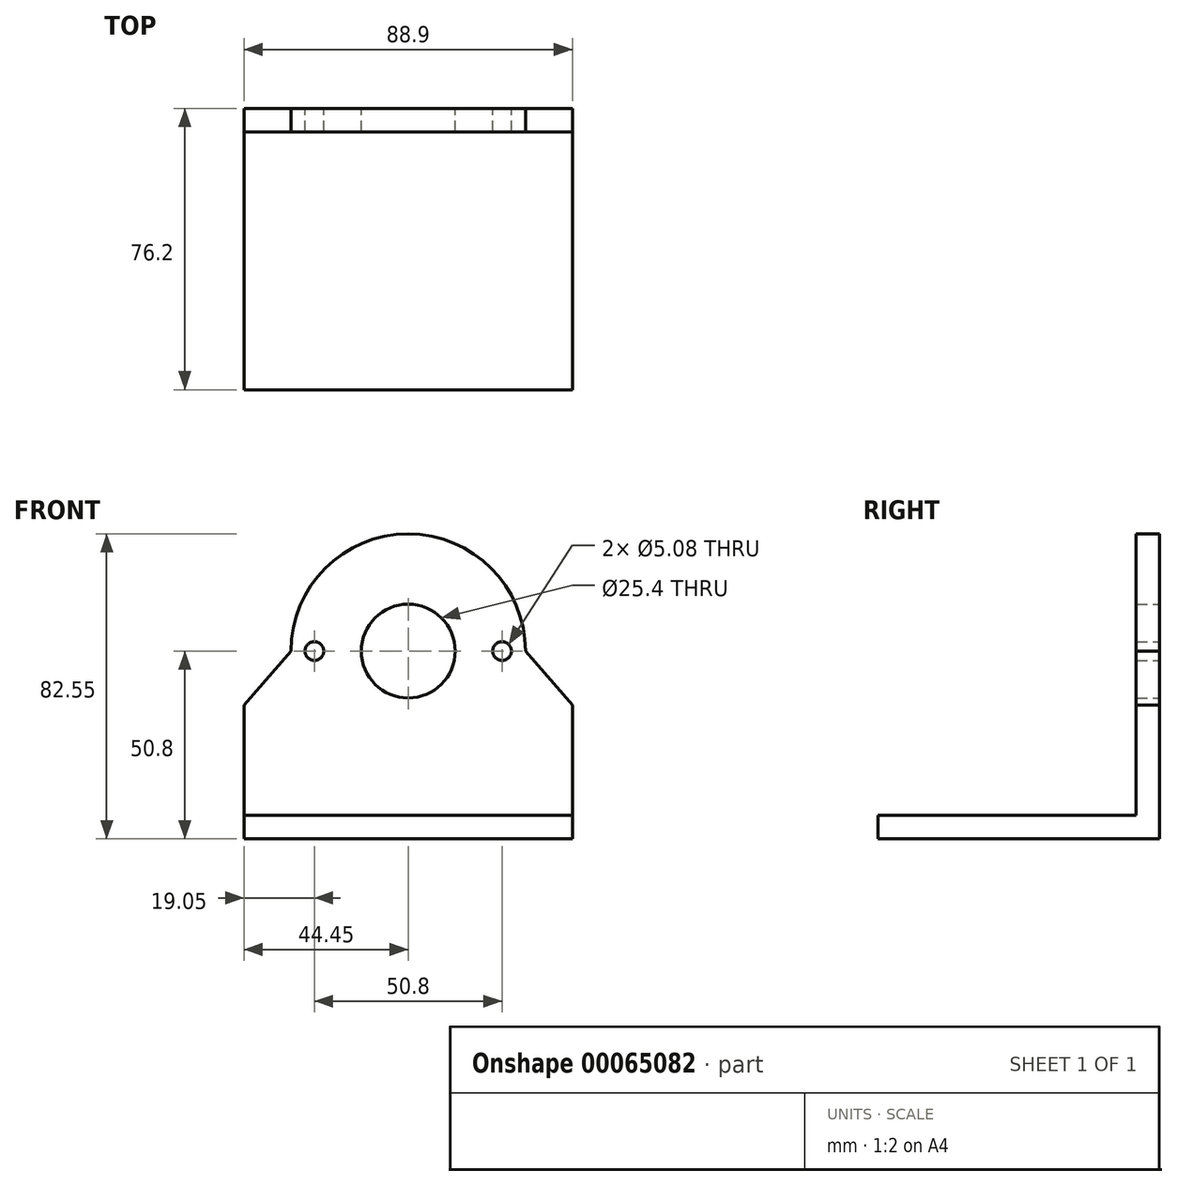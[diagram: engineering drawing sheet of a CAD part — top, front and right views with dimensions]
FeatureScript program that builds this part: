
annotation { "Feature Type Name" : "Feature", "Feature Type Description" : "" }
export const myFeature = defineFeature(function(context is Context, id is Id, definition is map)
    precondition{}
    {
        {
            var Q0;
            Q0=qCreatedBy(makeId("Front.planeOp"),FACE);
            var sketch = newSketch(context, id + "F0", { "sketchPlane" : qUnion([Q0])});
            skCircle(sketch, "E0", {"center": v(0, 0) * mm, "radius": 12.7 * mm});
            skCircle(sketch, "E1", {"center": v(0, 0) * mm, "radius": 25.4 * mm, "construction": true});
            skLineSegment(sketch, "E2", {"start": v(-46.37, 0) * mm, "end": v(56.92, 0) * mm, "construction": true});
            skCircle(sketch, "E3", {"center": v(-25.4, 0) * mm, "radius": 2.54 * mm});
            skCircle(sketch, "E4", {"center": v(25.4, 0) * mm, "radius": 2.54 * mm});
            skCircle(sketch, "E5", {"center": v(0, 0) * mm, "radius": 31.75 * mm});
            skLineSegment(sketch, "E6.rect.bottom", {"start": v(-44.45, 44.45) * mm, "end": v(44.45, 44.45) * mm});
            skLineSegment(sketch, "E6.rect.top", {"start": v(-44.45, -44.45) * mm, "end": v(44.45, -44.45) * mm});
            skLineSegment(sketch, "E6.rect.left", {"start": v(-44.45, 44.45) * mm, "end": v(-44.45, -44.45) * mm});
            skLineSegment(sketch, "E6.rect.right", {"start": v(44.45, 44.45) * mm, "end": v(44.45, -44.45) * mm});
            skLineSegment(sketch, "E7", {"start": v(-31.75, 0) * mm, "end": v(-44.45, -14.6) * mm});
            skLineSegment(sketch, "E8", {"start": v(31.75, 0) * mm, "end": v(44.45, -14.6) * mm});
            skLineSegment(sketch, "E9.top", {"start": v(-44.45, -50.8) * mm, "end": v(44.45, -50.8) * mm});
            skLineSegment(sketch, "E9.left", {"start": v(-44.45, -44.45) * mm, "end": v(-44.45, -50.8) * mm});
            skLineSegment(sketch, "E9.right", {"start": v(44.45, -44.45) * mm, "end": v(44.45, -50.8) * mm});
            skSolve(sketch);
        }
        {
            var Q0;
            Q0=makeQuery(id+"F0.imprint","IMPRINT",FACE,{"disambiguationData":[TD([[makeQuery(id+"F0.imprint","IMPRINT",EDGE,{"derivedFrom":sQuery(id+"F0.wireOp",EDGE,"E6.rect.top")}),-1.0]])]});
            var Q1;
            {var subQ0=sQuery(id+"F0.wireOp",EDGE,"E7");Q1=makeQuery(id+"F0.imprint","IMPRINT",FACE,{"disambiguationData":[TD([[makeQuery(id+"F0.imprint","IMPRINT",EDGE,{"derivedFrom":subQ0}),1.0]])]});}
            var Q2;
            Q2=makeQuery(id+"F0.imprint","IMPRINT",FACE,{"disambiguationData":[TD([[makeQuery(id+"F0.imprint","IMPRINT",EDGE,{"derivedFrom":sQuery(id+"F0.wireOp",EDGE,"E0")}),-1.0]])]});
            extrude(context, id + "F1", {"entities" : qUnion([Q0, Q1, Q2]), "depth" : 6.35 * mm});
        }
        {
            var Q0;
            Q0=makeQuery(id+"F0.imprint","IMPRINT",FACE,{"disambiguationData":[TD([[makeQuery(id+"F0.imprint","IMPRINT",EDGE,{"derivedFrom":sQuery(id+"F0.wireOp",EDGE,"E6.rect.top")}),-1.0]])]});
            extrude(context, id + "F2", {"entities" : qUnion([Q0]), "operationType" : NewBodyOperationType.ADD, "depth" : 76.2 * mm});
        }
    });
